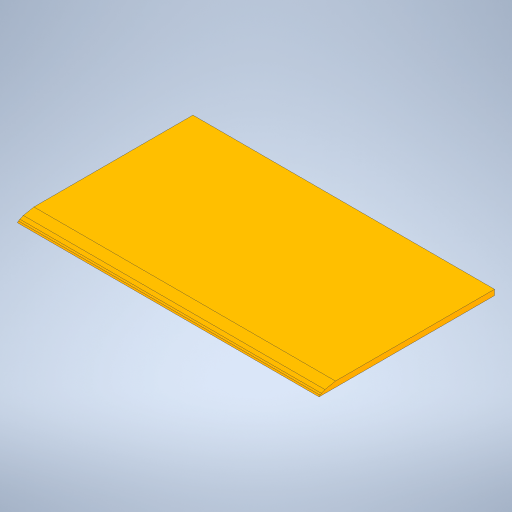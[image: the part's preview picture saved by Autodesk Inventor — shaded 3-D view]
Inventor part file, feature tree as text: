
AUTODESK INVENTOR PART (.ipt)
format: ipt  version: 2024 (Build 280153000, 153)  size: 243,712 bytes
history: native  units: mm
features: chamfer x4, extrude x2, sketch x2
ambient origin geometry x8: Origin, YZ Plane, XZ Plane, XY Plane, X Axis, Y Axis, Z Axis, Center Point
bodies: Solid1 (feature_tree)
feature tree (8):
  extrude  "Extrusion1"  Depth=110.0mm
  extrude  "Extrusion2"  Depth=2.0mm TaperAngle=0.0deg
  chamfer  "Chamfer4"  Distance=2.0mm Angle=45.0deg
  chamfer  "Chamfer5"  Distance=2.0mm Angle=45.0deg
  chamfer  "Chamfer6"  Distance=2.0mm Angle=45.0deg
  chamfer  "Chamfer7"  Distance=2.0mm Angle=45.0deg
  sketch  "Sketch1"  dims[d0=110.0mm d1=50.0mm]
  sketch  "Sketch2"  dims[d2=2.0mm d3=0.0mm d13=14.0mm d14=0.0mm d15=2.0mm d16=2.0mm d17=45.0deg d18=2.0mm d19=2.0mm d20=45.0deg d21=2.0mm d22=2.0mm d23=45.0deg d24=0.3mm d25=2.0mm d26=45.0deg]
